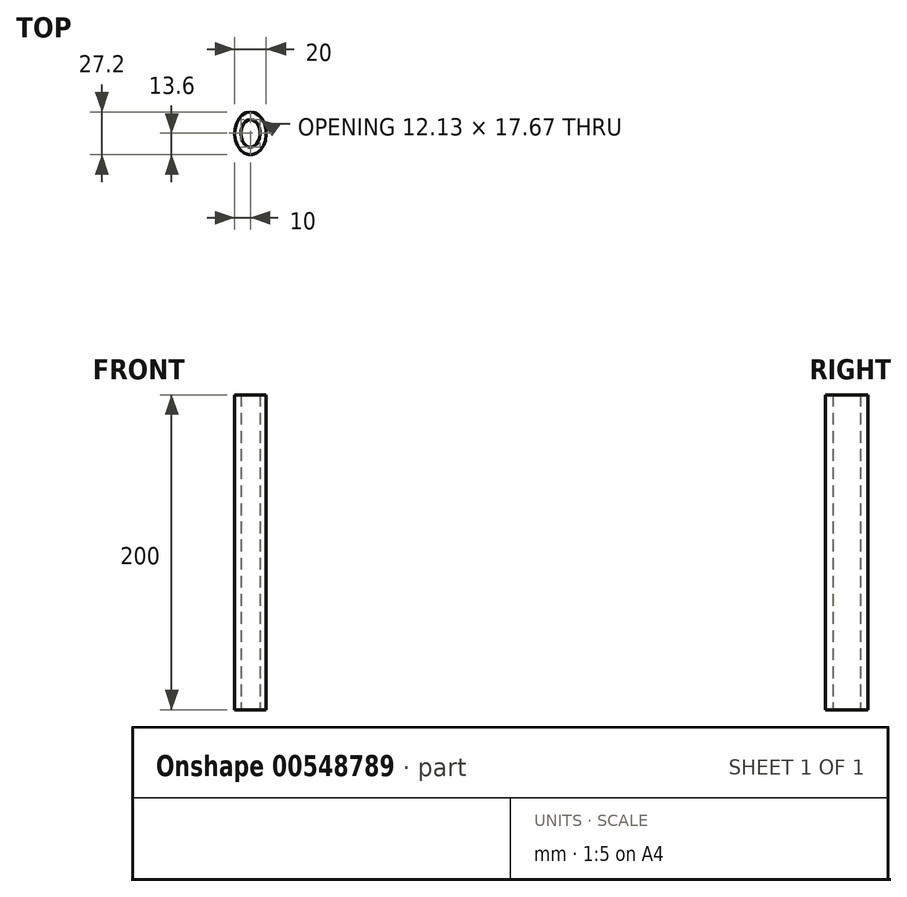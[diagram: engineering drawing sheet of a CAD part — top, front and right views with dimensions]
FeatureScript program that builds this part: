
annotation { "Feature Type Name" : "Feature", "Feature Type Description" : "" }
export const myFeature = defineFeature(function(context is Context, id is Id, definition is map)
    precondition{}
    {
        {
            var Q0;
            Q0=qCreatedBy(makeId("Top.planeOp"),FACE);
            var sketch = newSketch(context, id + "F0", { "sketchPlane" : qUnion([Q0])});
            skEllipse(sketch, "E0", {"center": v(0, 0) * mm, "majorRadius": 13.6 * mm, "minorRadius": 10 * mm, "majorAxis": v(0, 1)});
            skEllipse(sketch, "E1", {"center": v(0, 0) * mm, "majorRadius": 8.84 * mm, "minorRadius": 6.06 * mm, "majorAxis": v(0, 1)});
            skSolve(sketch);
        }
        {
            var Q0;
            Q0=makeQuery(id+"F0.imprint","IMPRINT",FACE,{"disambiguationData":[TD([[makeQuery(id+"F0.imprint","IMPRINT",EDGE,{"derivedFrom":sQuery(id+"F0.wireOp",EDGE,"E0")}),1.0]])]});
            extrude(context, id + "F1", {"entities" : qUnion([Q0]), "depth" : 200 * mm, "offsetDistance" : 25 * mm});
        }
    });
